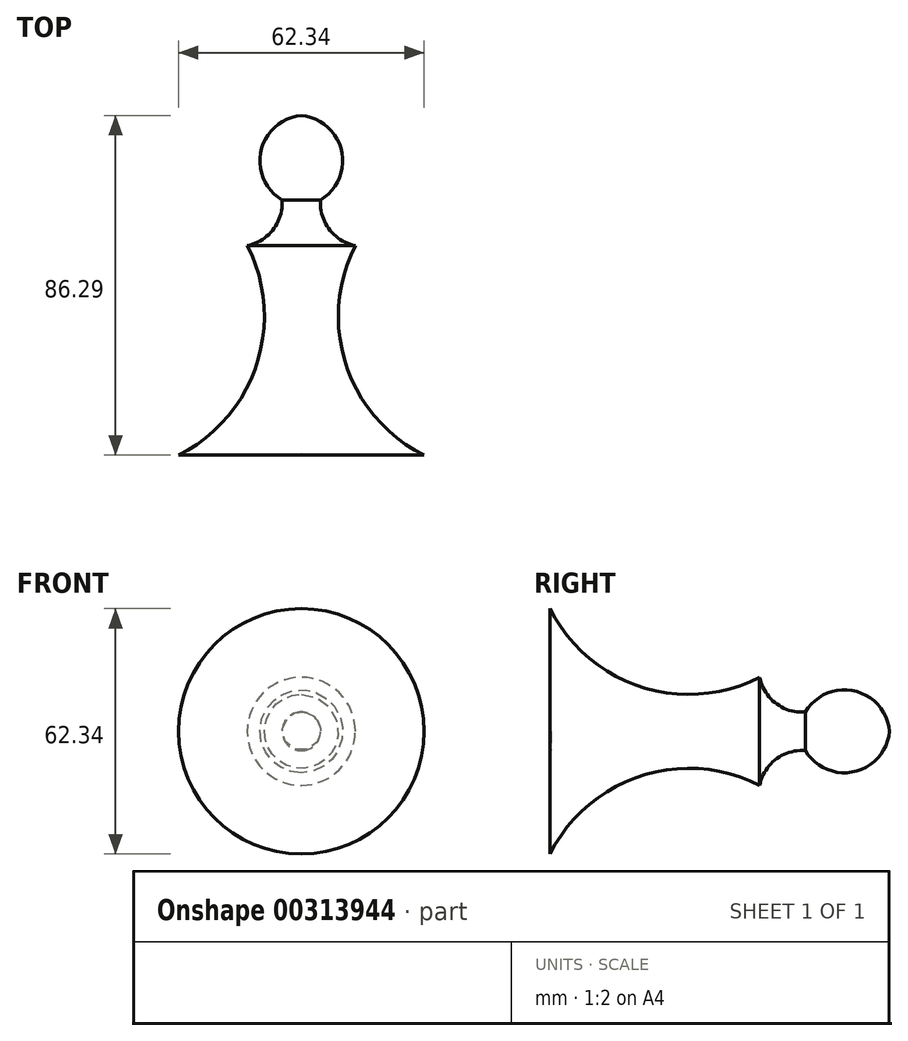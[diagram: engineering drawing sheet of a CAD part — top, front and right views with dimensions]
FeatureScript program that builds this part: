
annotation { "Feature Type Name" : "Feature", "Feature Type Description" : "" }
export const myFeature = defineFeature(function(context is Context, id is Id, definition is map)
    precondition{}
    {
        {
            var Q0;
            Q0=qCreatedBy(makeId("Top.planeOp"),FACE);
            var sketch = newSketch(context, id + "F0", { "sketchPlane" : qUnion([Q0])});
            skLineSegment(sketch, "E0", {"start": v(0, 37.91) * mm, "end": v(0, -48.15) * mm});
            skArc(sketch, "E1", {"start": v(0, 14.89) * mm, "mid": v(10.53, 26.4) * mm, "end": v(0, 37.91) * mm});
            skArc(sketch, "E2", {"start": v(4.9, 16.48) * mm, "mid": v(7.1, 9) * mm, "end": v(13.72, 4.88) * mm});
            skArc(sketch, "E3", {"start": v(13.72, 4.88) * mm, "mid": v(11.36, -25.38) * mm, "end": v(31.17, -48.38) * mm});
            skLineSegment(sketch, "E4", {"start": v(31.17, -48.38) * mm, "end": v(0, -48.15) * mm});
            skSolve(sketch);
        }
        {
            var Q0;
            Q0 = qSketchRegion(id + "F0", true);
            var Q1;
            Q1=sQuery(id+"F0.wireOp",EDGE,"E0");
            revolve(context, id + "F1", {"entities" : qUnion([Q0]), "axis" : qUnion([Q1]), "revolveType" : RevolveType.FULL});
        }
    });
